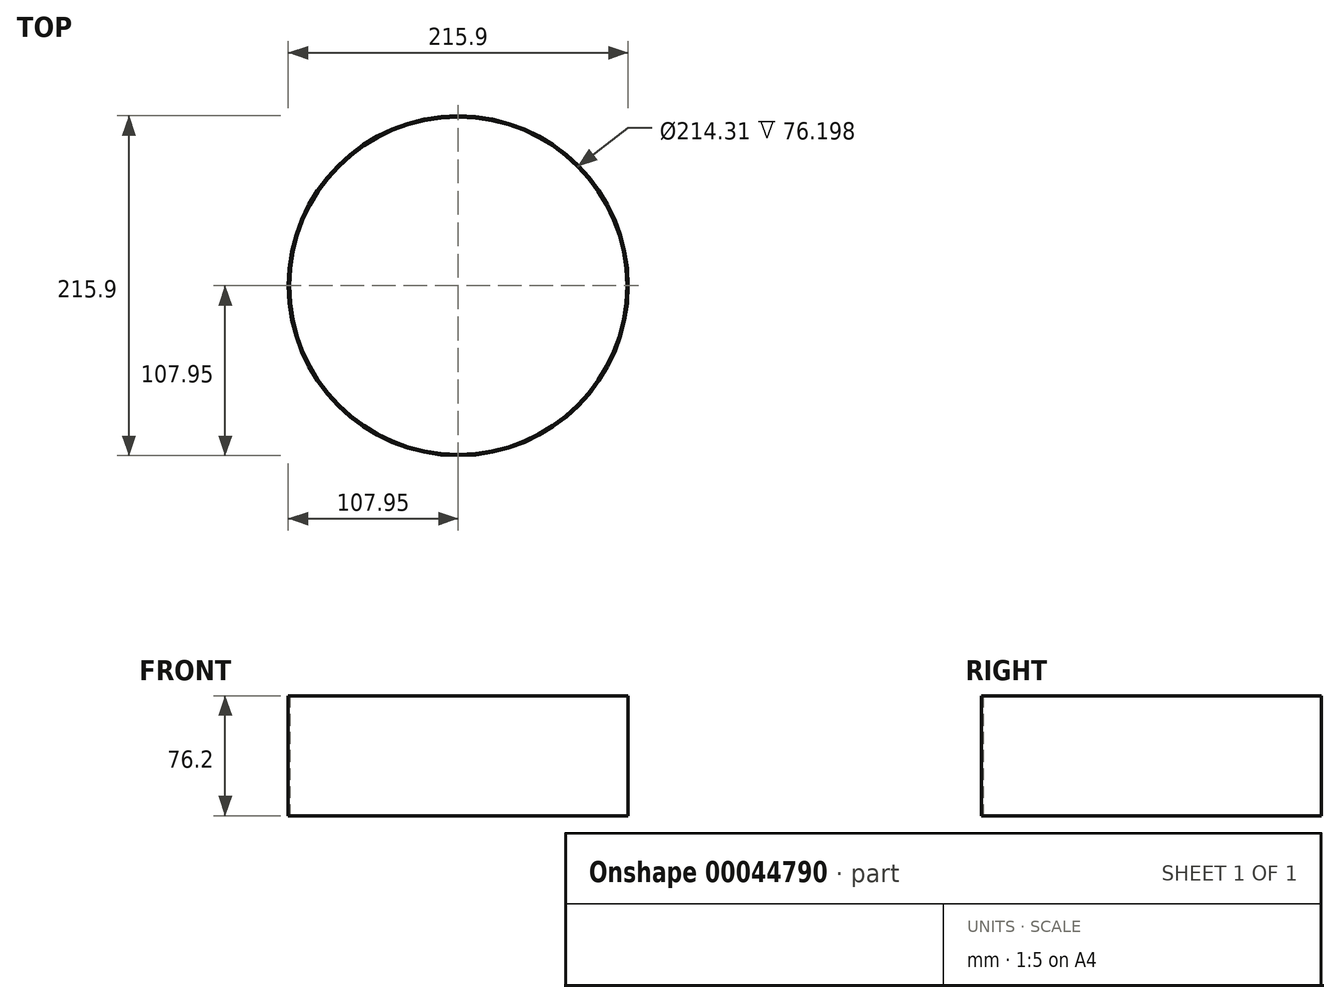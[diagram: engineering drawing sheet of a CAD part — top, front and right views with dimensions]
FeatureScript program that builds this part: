
annotation { "Feature Type Name" : "Feature", "Feature Type Description" : "" }
export const myFeature = defineFeature(function(context is Context, id is Id, definition is map)
    precondition{}
    {
        {
            var Q0;
            Q0=qCreatedBy(makeId("Top.planeOp"),FACE);
            var sketch = newSketch(context, id + "F0", { "sketchPlane" : qUnion([Q0])});
            skCircle(sketch, "E0", {"center": v(0, 0) * mm, "radius": 107.95 * mm});
            skCircle(sketch, "E1", {"center": v(0, 0) * mm, "radius": 107.16 * mm});
            skSolve(sketch);
        }
        {
            var Q0;
            Q0=makeQuery(id+"F0.imprint","IMPRINT",FACE,{"disambiguationData":[TD([[makeQuery(id+"F0.imprint","IMPRINT",EDGE,{"derivedFrom":sQuery(id+"F0.wireOp",EDGE,"E0")}),1.0]])]});
            extrude(context, id + "F1", {"entities" : qUnion([Q0]), "depth" : 76.2 * mm});
        }
        {
            var Q0;
            Q0=makeQuery(id+"F0.imprint","IMPRINT",FACE,{"disambiguationData":[TD([[makeQuery(id+"F0.imprint","IMPRINT",EDGE,{"derivedFrom":sQuery(id+"F0.wireOp",EDGE,"E1")}),1.0]])]});
            extrude(context, id + "F2", {"entities" : qUnion([Q0]), "operationType" : NewBodyOperationType.ADD, "depth" : 1 / 406.4 * mm});
        }
    });
